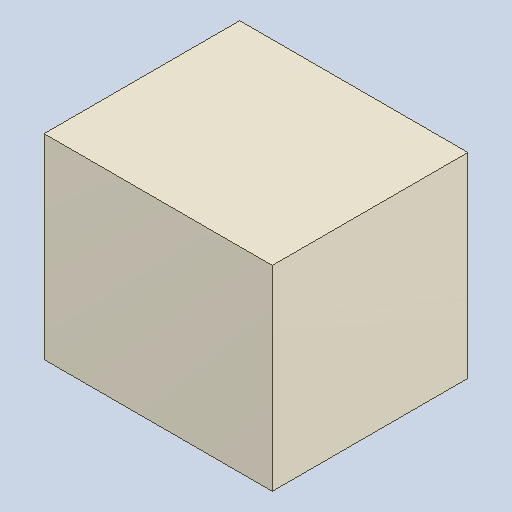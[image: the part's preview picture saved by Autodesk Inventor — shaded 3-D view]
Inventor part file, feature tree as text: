
AUTODESK INVENTOR PART (.ipt)
format: ipt  version: 2023.4 (Build 274418000, 418)  size: 82,432 bytes
history: native  units: mm
features: extrude x1
ambient origin geometry x8: Origin, YZ Plane, XZ Plane, XY Plane, X Axis, Y Axis, Z Axis, Center Point
bodies: Solid1 (feature_tree)
feature tree (1):
  extrude  "Extruded_16"  [1 undecoded]
note: 1 required parameter value undecoded (feature->parameter linkage not recoverable at this tier; creation-order binding heuristic only, values carry confidence <= 0.55)
